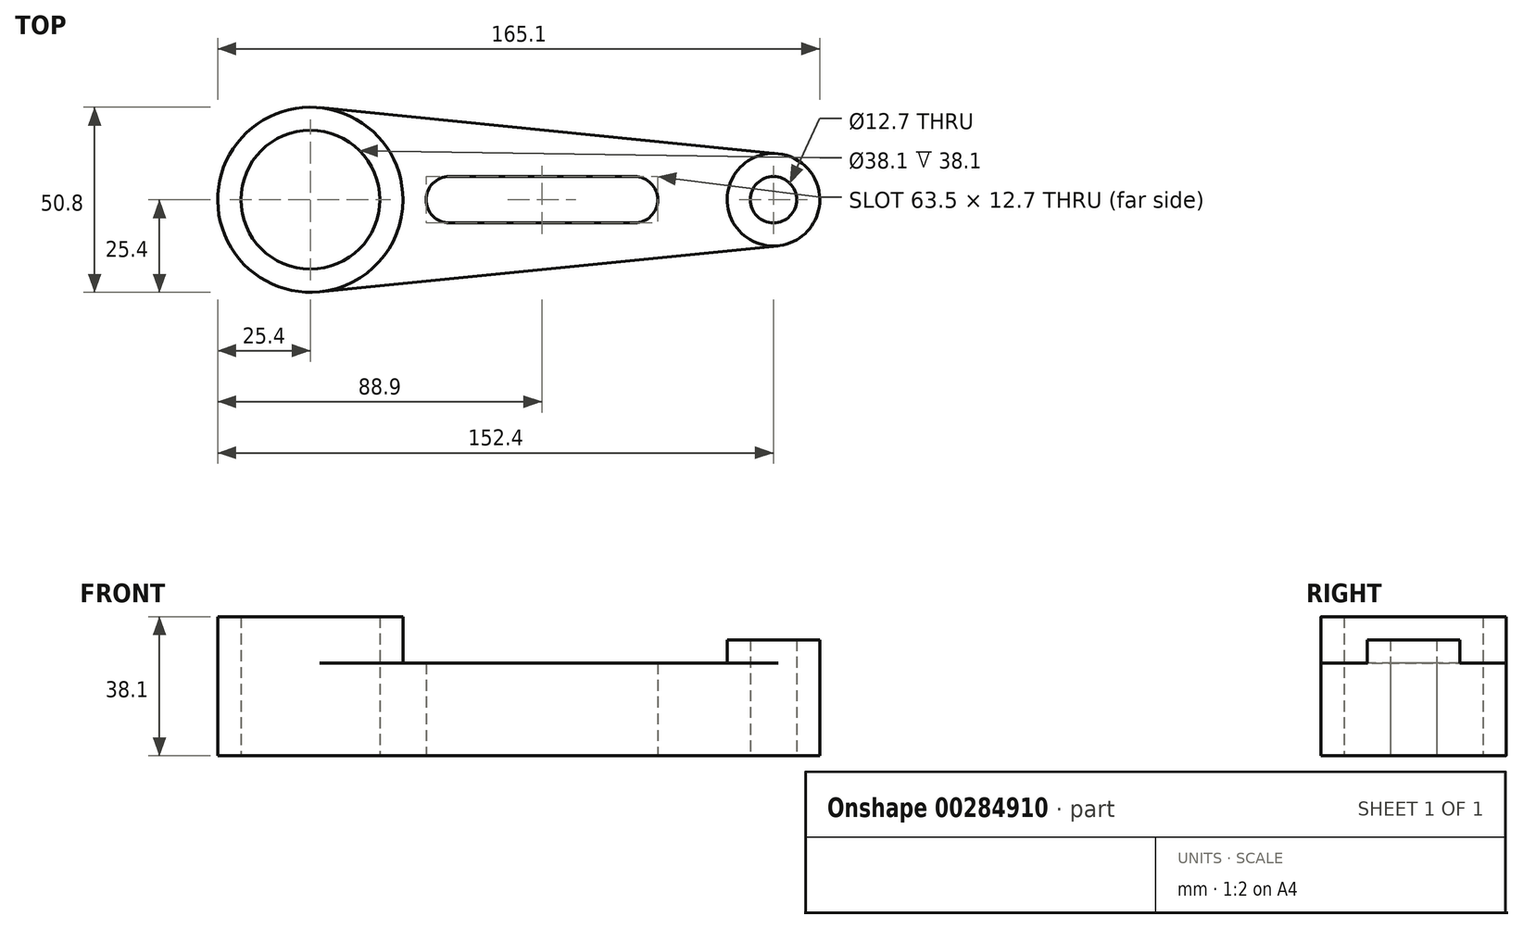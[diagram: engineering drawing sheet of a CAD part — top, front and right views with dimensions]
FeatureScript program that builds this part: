
annotation { "Feature Type Name" : "Feature", "Feature Type Description" : "" }
export const myFeature = defineFeature(function(context is Context, id is Id, definition is map)
    precondition{}
    {
        {
            var Q0;
            Q0=qCreatedBy(makeId("Top.planeOp"),FACE);
            var sketch = newSketch(context, id + "F0", { "sketchPlane" : qUnion([Q0])});
            skCircle(sketch, "E0", {"center": v(-38.1, 0) * mm, "radius": 19.05 * mm});
            skCircle(sketch, "E1", {"center": v(-38.1, 0) * mm, "radius": 25.4 * mm});
            skArc(sketch, "E2", {"start": v(0, 6.35) * mm, "mid": v(-6.35, 0) * mm, "end": v(0, -6.35) * mm});
            skArc(sketch, "E3", {"start": v(50.8, -6.35) * mm, "mid": v(57.15, 0) * mm, "end": v(50.8, 6.35) * mm});
            skCircle(sketch, "E4", {"center": v(88.9, 0) * mm, "radius": 6.35 * mm});
            skCircle(sketch, "E5", {"center": v(88.9, 0) * mm, "radius": 12.7 * mm});
            skLineSegment(sketch, "E6", {"start": v(90.17, -12.64) * mm, "end": v(-35.56, -25.27) * mm});
            skLineSegment(sketch, "E7", {"start": v(90.17, 12.64) * mm, "end": v(-35.56, 25.27) * mm});
            skLineSegment(sketch, "E8", {"start": v(0, -6.35) * mm, "end": v(50.8, -6.35) * mm});
            skLineSegment(sketch, "E9", {"start": v(0, 6.35) * mm, "end": v(50.8, 6.35) * mm});
            skSolve(sketch);
        }
        {
            var Q0;
            Q0=makeQuery(id+"F0.imprint","IMPRINT",FACE,{"disambiguationData":[TD([[makeQuery(id+"F0.imprint","IMPRINT",EDGE,{"derivedFrom":sQuery(id+"F0.wireOp",EDGE,"E4")}),-1.0]])]});
            extrude(context, id + "F1", {"entities" : qUnion([Q0]), "depth" : 31.75 * mm});
        }
        {
            var Q0;
            Q0=makeQuery(id+"F0.imprint","IMPRINT",FACE,{"disambiguationData":[TD([[makeQuery(id+"F0.imprint","IMPRINT",EDGE,{"derivedFrom":sQuery(id+"F0.wireOp",EDGE,"E2")}),-1.0]])]});
            extrude(context, id + "F2", {"entities" : qUnion([Q0]), "operationType" : NewBodyOperationType.ADD, "depth" : 25.4 * mm});
        }
        {
            var Q0;
            Q0=makeQuery(id+"F0.imprint","IMPRINT",FACE,{"disambiguationData":[TD([[makeQuery(id+"F0.imprint","IMPRINT",EDGE,{"derivedFrom":sQuery(id+"F0.wireOp",EDGE,"E0")}),-1.0]])]});
            extrude(context, id + "F3", {"entities" : qUnion([Q0]), "operationType" : NewBodyOperationType.ADD, "depth" : 38.1 * mm});
        }
    });
